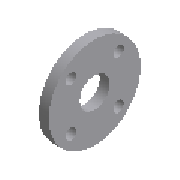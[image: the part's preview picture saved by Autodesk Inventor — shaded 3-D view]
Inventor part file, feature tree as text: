
AUTODESK INVENTOR PART (.ipt)
format: ipt  version: 2025 (Build 290162010, 162A)  size: 168,960 bytes
history: native  units: mm (DEFAULTED — no unit token found)
features: other x6, revolve x1, extrude x1, pattern_circular x1
ambient origin geometry x8: Origin, YZ Plane, XZ Plane, XY Plane, X Axis, Y Axis, Z Axis, Center Point
bodies: Solid1 (feature_tree)
feature tree (9):
  other  "DIN EN 1092-1 Plate Flange for Welding Type 01 - PN 25 80 x 88.9"
  revolve  "Revolution1"  Angle=90.0deg
  extrude  "Extrusion1"  Depth=200.0mm
  pattern_circular  "Circular Pattern1"  [2 undecoded]
  other  "Work Axis1"
  other  "Work Point1"
  other  "Work Axis2"
  other  "Work Point2"
  other  "Work Point3"
note: 2 required parameter values undecoded (feature->parameter linkage not recoverable at this tier; creation-order binding heuristic only, values carry confidence <= 0.55)
